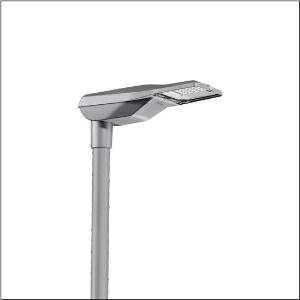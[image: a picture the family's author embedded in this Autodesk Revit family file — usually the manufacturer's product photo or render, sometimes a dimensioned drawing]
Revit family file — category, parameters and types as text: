
# Revit family: streetlight_sl_21_iq_micro___stw1_0a_5xe1e41g08db_19ca
name_source: partatom
category: Lighting Fixtures
units: mm (PartAtom-declared; Revit-internal decimal feet)

## family parameters
Cut with Voids When Loaded = No
Host = Face
Light Source = No
Part Type = Normal
Room Calculation Point = No
Round Connector Dimension = Use Diameter
Shared = No

## types (1)
- --- (1 x LED, 5010 lm, 36.4 W, 4000K)
    Apparent Load = 36 VA
    CIE Flux Codes = 38 75 98 100 100
    Color Rendering = 70
    Color Temperature = 4000K
    Default Elevation = 1800 mm
    Description = Streetlight SL 21 iQ micro, mast luminaire, primary light control with lens, of PMMA, primary optical cover: cover, of toughened safety glass, transparent, light distribution: STW1.0a, light emission: direct distribution, primary light characteristic: asymmetric, installation type: post-top, side-entry, LED, High Power LED, rated luminous flux: 5.010lm, luminous efficacy: 138lm/W, light colour: 740, colour temperature: 4000K, control gear: iQ Street-Remote, control: Street-Remote, Auto-Match, Temp-Guard, Lumen-Switch, Night-Set, Smart-Wire, Light-Fading, Desk-Remote (wireless, voltage-free reading and setting of iQ features in the workshop via application-optimized NFC function/RFID function), optimised constant luminous flux control (CLO 2.0), pre-setting: linear dimming characteristic, mains connection: 220..240V, AC, 50/60Hz, start of lifetime: 36W, end of service life: 38W, reduction: 16W, luminaire housing, of diecast aluminium, powder-coated, Siteco® metallic grey (DB 702S), corrosivity category C5 high according to DIN EN ISO 12944, please order mast flange separately, inclination adjustable: 0°, 5°, 10°, 15°, sealing non-destructively replaceable, multi-level sealing system, length: 528mm, width: 235mm, height: 110mm, mast flange for spigot size: 42mm (side-entry): 5XC10008XM4, 60/48mm (side-entry/post-top): 5XC10108XM2, 76/60mm (side-entry/post-top): 5XC10108XM1, protection rating (complete): IP66, insulation class (complete): insulation class II (safety insulation), certification: CE, ENEC, ENEC+, VDE, impact resistance: IK10, permissible operating ambient temperature for outdoor applications: -40..+50°C, standard-compliant lighting for roads and squares, packaging unit: 1 piece

Light Distribution: STW1.0a
    Height = 110 mm
    Lamp = 1 x LED
    Lamp Light Flux = 5010 lm
    Lamp Power = 36.4 W
    Lamp count = 1
    Length = 528 mm
    Luminous efficacy = 138 lm/W
    Manufacturer = Siteco
    ModVariant = No
    Model = 5XE1E41G08DB
    Number of Poles = 1
    OnlyDefault = Yes
    Power Factor = 1
    Product Name = Streetlight SL 21 iQ micro | STW1.0a
    Product group = mast luminaire | pylon top
    ProductGroupID = 6100
    Protection Class = Protection class II
    Protection Degree = IP 66
    RLX_Detail_Level = 1
    RLX_Emergency_Light_Flux = 0 lm
    RLX_Emergency_Type = 0
    RLX_Emergency_Type_DB = No
    RlxData = <blob elided: 99565 chars, md5=de71e70b>
    Socket = socket
    Standby Power = 0 W
    System Light Flux = 5010 lm
    System Power = 36 W
    Type Comments = factory setting: luminous flux: 100 % | dim-lin: 254 | 715 mA
    Type Image = l_1006881.jpg
    URL = http://relux.com
    VarID = @adj_158659
    Voltage = 0 V
    Weight = 0.00 kg
    Width = 235 mm

## geometry (parser evidence)
native form markers: Blend x4, Sweep x11
no freeform markers — native parametric forms only
